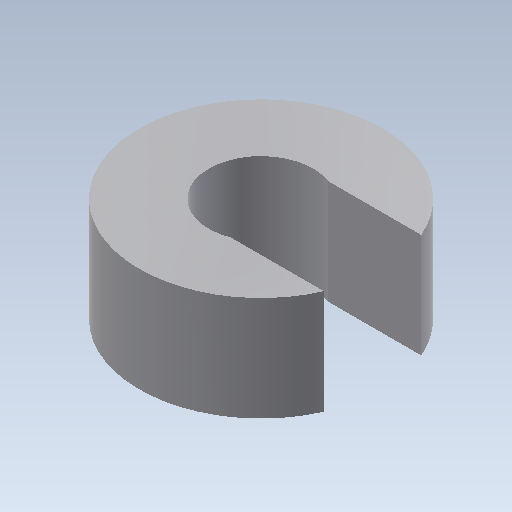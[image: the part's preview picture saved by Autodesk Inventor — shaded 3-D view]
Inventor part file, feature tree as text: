
AUTODESK INVENTOR PART (.ipt)
format: ipt  version: 2020 (Build 240168000, 168)  size: 90,112 bytes
history: native  units: mm
features: extrude x1, sketch x1
ambient origin geometry x8: Origin, YZ Plane, XZ Plane, XY Plane, X Axis, Y Axis, Z Axis, Center Point
bodies: Solid1 (feature_tree)
feature tree (2):
  extrude  "Extrusion1"  Depth=2.8mm
  sketch  "Sketch1"  dims[d0=7.0mm d1=2.8mm d2=1.5mm d3=3.0mm d4=0.0mm]
